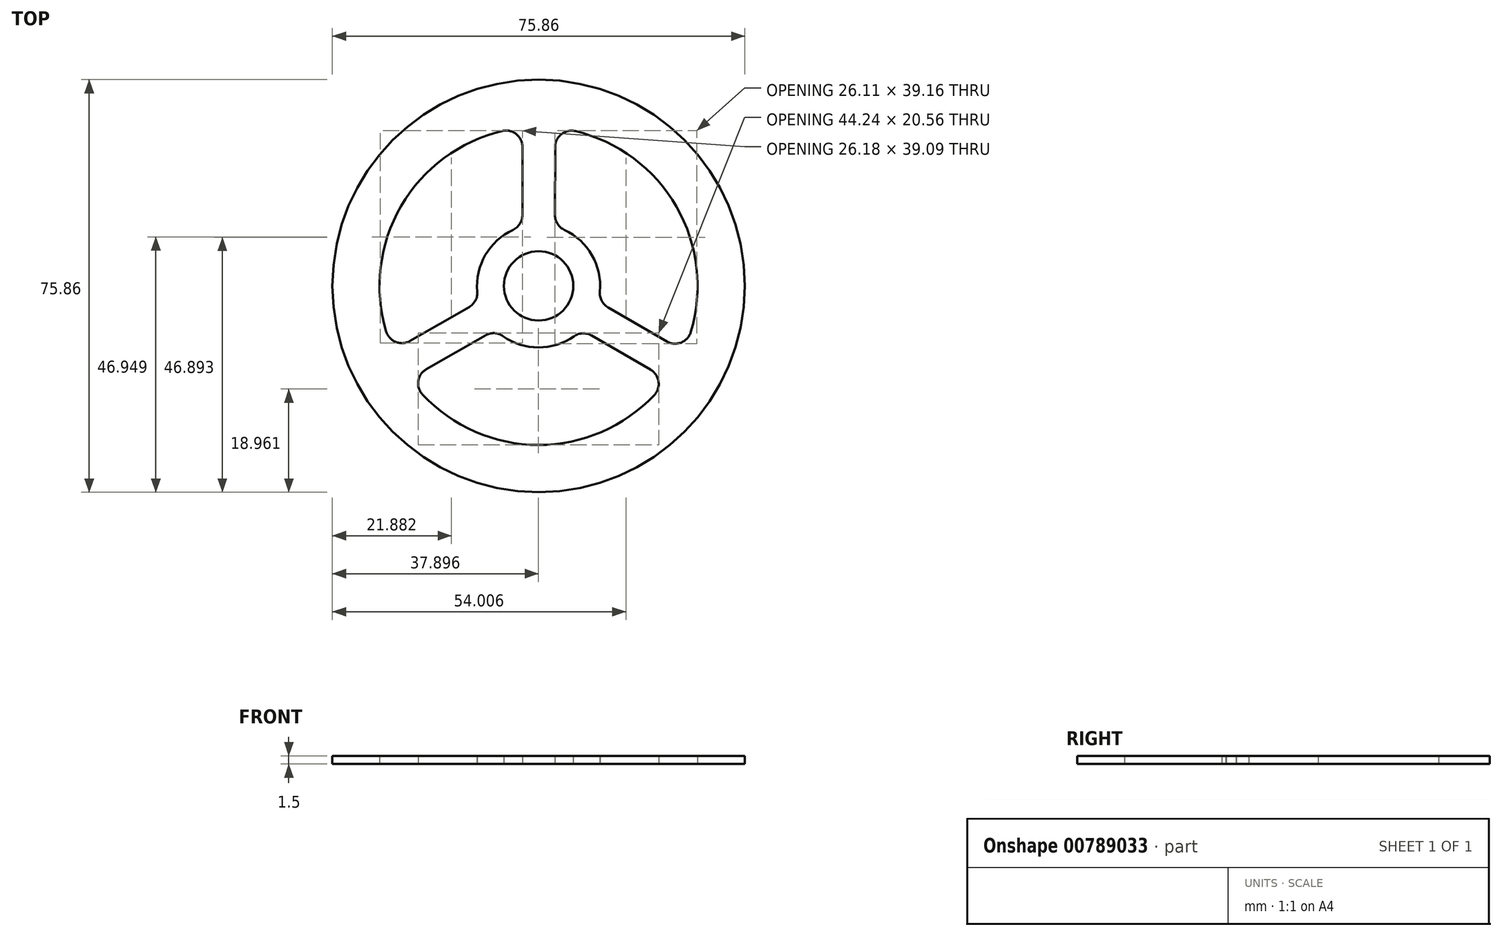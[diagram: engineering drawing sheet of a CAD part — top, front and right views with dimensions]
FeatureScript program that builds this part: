
annotation { "Feature Type Name" : "Feature", "Feature Type Description" : "" }
export const myFeature = defineFeature(function(context is Context, id is Id, definition is map)
    precondition{}
    {
        {
            var Q0;
            Q0=qCreatedBy(makeId("Top.planeOp"),FACE);
            var sketch = newSketch(context, id + "F0", { "sketchPlane" : qUnion([Q0])});
            skCircle(sketch, "E0", {"center": v(0, 0) * mm, "radius": 37.92 * mm});
            skCircle(sketch, "E1", {"center": v(0, 0) * mm, "radius": 29.25 * mm});
            skCircle(sketch, "E2", {"center": v(0, 0) * mm, "radius": 11.32 * mm});
            skPoint(sketch, "E3.0.midPoint", {"position": v(12.68, 7.29) * mm});
            skPoint(sketch, "E4", {"position": v(0.05, 29.25) * mm});
            skPoint(sketch, "E5", {"position": v(25.3, -14.67) * mm});
            skPoint(sketch, "E6", {"position": v(-25.36, -14.58) * mm});
            skLineSegment(sketch, "E7", {"start": v(-26.72, -11.9) * mm, "end": v(-10.96, -2.84) * mm});
            skLineSegment(sketch, "E8", {"start": v(7.94, -8.07) * mm, "end": v(23.67, -17.2) * mm});
            skLineSegment(sketch, "E9", {"start": v(26.68, -12) * mm, "end": v(10.95, -2.88) * mm});
            skLineSegment(sketch, "E10", {"start": v(3.02, 10.92) * mm, "end": v(3.05, 29.1) * mm});
            skLineSegment(sketch, "E11", {"start": v(-2.95, 29.1) * mm, "end": v(-2.98, 10.93) * mm});
            skLineSegment(sketch, "E12", {"start": v(-23.73, -17.1) * mm, "end": v(-7.97, -8.04) * mm});
            skCircle(sketch, "E13", {"center": v(0, 0) * mm, "radius": 6.38 * mm});
            skCircle(sketch, "E14", {"center": v(0, 0) * mm, "radius": 3 * mm});
            skSolve(sketch);
        }
        {
            var Q0;
            Q0 = qSketchRegion(id + "F0", true);
            var Q1;
            {var subQ0=sQuery(id+"F0.wireOp",EDGE,"E10");Q1=makeQuery(id+"F0.imprint","IMPRINT",FACE,{"disambiguationData":[TD([[makeQuery(id+"F0.imprint","IMPRINT",EDGE,{"derivedFrom":subQ0}),1.0]])]});}
            var Q2;
            Q2=makeQuery(id+"F0.imprint","IMPRINT",FACE,{"disambiguationData":[TD([[makeQuery(id+"F0.imprint","IMPRINT",EDGE,{"derivedFrom":sQuery(id+"F0.wireOp",EDGE,"E13")}),-1.0]])]});
            var Q3;
            {var subQ0=sQuery(id+"F0.wireOp",EDGE,"E7");Q3=makeQuery(id+"F0.imprint","IMPRINT",FACE,{"disambiguationData":[TD([[makeQuery(id+"F0.imprint","IMPRINT",EDGE,{"derivedFrom":subQ0}),-1.0]])]});}
            var Q4;
            {var subQ0=sQuery(id+"F0.wireOp",EDGE,"E8");Q4=makeQuery(id+"F0.imprint","IMPRINT",FACE,{"disambiguationData":[TD([[makeQuery(id+"F0.imprint","IMPRINT",EDGE,{"derivedFrom":subQ0}),1.0]])]});}
            extrude(context, id + "F1", {"entities" : qUnion([Q0, Q1, Q2, Q3, Q4]), "depth" : 1.5 * mm, "offsetDistance" : 25 * mm});
        }
        {
            var Q0;
            Q0=makeQuery(id+"F1.opExtrude","SWEPT_EDGE",EDGE,{"disambiguationData":[OSD([sQuery(id+"F0.wireOp",EDGE,"E2"),sQuery(id+"F0.wireOp",EDGE,"E12")])]});
            var Q1;
            Q1=makeQuery(id+"F1.opExtrude","SWEPT_EDGE",EDGE,{"disambiguationData":[OSD([sQuery(id+"F0.wireOp",EDGE,"E1"),sQuery(id+"F0.wireOp",EDGE,"E12")])]});
            var Q2;
            Q2=makeQuery(id+"F1.opExtrude","SWEPT_EDGE",EDGE,{"disambiguationData":[OSD([sQuery(id+"F0.wireOp",EDGE,"E2"),sQuery(id+"F0.wireOp",EDGE,"E8")])]});
            var Q3;
            Q3=makeQuery(id+"F1.opExtrude","SWEPT_EDGE",EDGE,{"disambiguationData":[OSD([sQuery(id+"F0.wireOp",EDGE,"E1"),sQuery(id+"F0.wireOp",EDGE,"E10")])]});
            var Q4;
            Q4=makeQuery(id+"F1.opExtrude","SWEPT_EDGE",EDGE,{"disambiguationData":[OSD([sQuery(id+"F0.wireOp",EDGE,"E1"),sQuery(id+"F0.wireOp",EDGE,"E8")])]});
            var Q5;
            Q5=makeQuery(id+"F1.opExtrude","SWEPT_EDGE",EDGE,{"disambiguationData":[OSD([sQuery(id+"F0.wireOp",EDGE,"E1"),sQuery(id+"F0.wireOp",EDGE,"E9")])]});
            var Q6;
            Q6=makeQuery(id+"F1.opExtrude","SWEPT_EDGE",EDGE,{"disambiguationData":[OSD([sQuery(id+"F0.wireOp",EDGE,"E1"),sQuery(id+"F0.wireOp",EDGE,"E11")])]});
            var Q7;
            Q7=makeQuery(id+"F1.opExtrude","SWEPT_EDGE",EDGE,{"disambiguationData":[OSD([sQuery(id+"F0.wireOp",EDGE,"E1"),sQuery(id+"F0.wireOp",EDGE,"E7")])]});
            var Q8;
            Q8=makeQuery(id+"F1.opExtrude","SWEPT_EDGE",EDGE,{"disambiguationData":[OSD([sQuery(id+"F0.wireOp",EDGE,"E2"),sQuery(id+"F0.wireOp",EDGE,"E11")])]});
            var Q9;
            Q9=makeQuery(id+"F1.opExtrude","SWEPT_EDGE",EDGE,{"disambiguationData":[OSD([sQuery(id+"F0.wireOp",EDGE,"E2"),sQuery(id+"F0.wireOp",EDGE,"E7")])]});
            var Q10;
            Q10=makeQuery(id+"F1.opExtrude","SWEPT_EDGE",EDGE,{"disambiguationData":[OSD([sQuery(id+"F0.wireOp",EDGE,"E2"),sQuery(id+"F0.wireOp",EDGE,"E9")])]});
            var Q11;
            Q11=makeQuery(id+"F1.opExtrude","SWEPT_EDGE",EDGE,{"disambiguationData":[OSD([sQuery(id+"F0.wireOp",EDGE,"E2"),sQuery(id+"F0.wireOp",EDGE,"E10")])]});
            fillet(context, id + "F2", {"entities" : qUnion([Q0, Q1, Q2, Q3, Q4, Q5, Q6, Q7, Q8, Q9, Q10, Q11]), "radius" : 3 * mm, "tangentPropagation" : true, "allowEdgeOverflow" : false});
        }
    });
